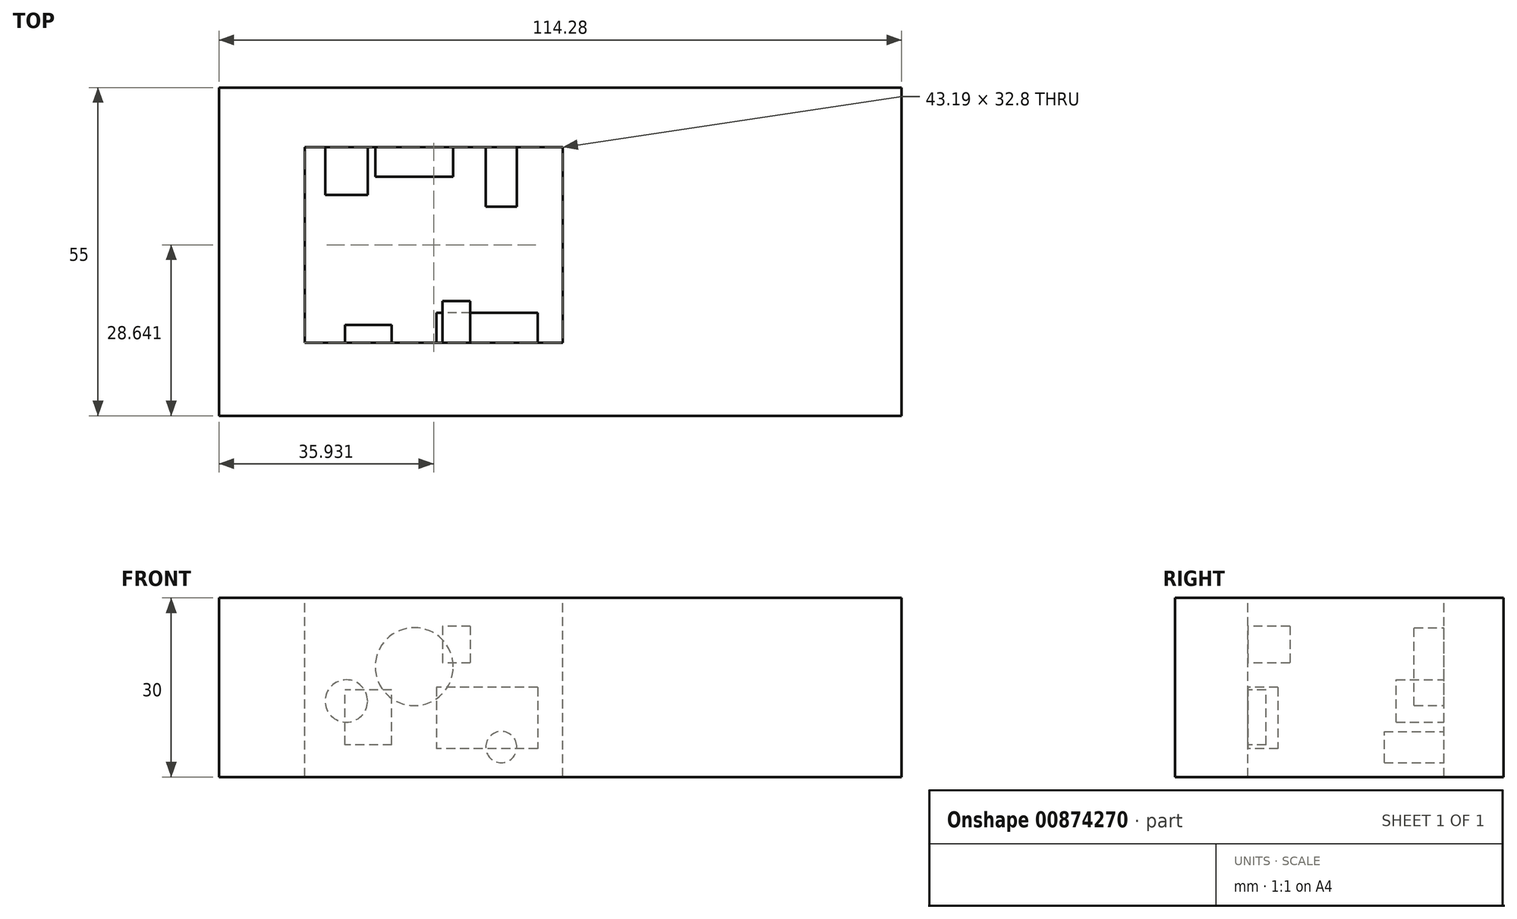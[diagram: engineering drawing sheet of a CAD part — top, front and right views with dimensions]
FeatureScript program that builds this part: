
annotation { "Feature Type Name" : "Feature", "Feature Type Description" : "" }
export const myFeature = defineFeature(function(context is Context, id is Id, definition is map)
    precondition{}
    {
        {
            var Q0;
            Q0=qCreatedBy(makeId("Top.planeOp"),FACE);
            var sketch = newSketch(context, id + "F0", { "sketchPlane" : qUnion([Q0])});
            skLineSegment(sketch, "E0.bottom", {"start": v(-114.28, 55) * mm, "end": v(0, 55) * mm});
            skLineSegment(sketch, "E0.top", {"start": v(-114.28, 0) * mm, "end": v(0, 0) * mm});
            skLineSegment(sketch, "E0.left", {"start": v(-114.28, 55) * mm, "end": v(-114.28, 0) * mm});
            skLineSegment(sketch, "E0.right", {"start": v(0, 55) * mm, "end": v(0, 0) * mm});
            skSolve(sketch);
        }
        {
            var Q0;
            Q0=makeQuery(id+"F0.imprint","IMPRINT",FACE,{"disambiguationData":[TD([[makeQuery(id+"F0.imprint","IMPRINT",EDGE,{"derivedFrom":sQuery(id+"F0.wireOp",EDGE,"E0.bottom")}),-1.0]])]});
            extrude(context, id + "F1", {"entities" : qUnion([Q0]), "depth" : 30 * mm, "offsetDistance" : 25 * mm});
        }
        {
            var Q0;
            Q0=makeQuery(id+"F1.opExtrude","CAP_FACE",FACE,{"disambiguationData":[OSD([sQuery(id+"F0.wireOp",EDGE,"E0.bottom"),sQuery(id+"F0.wireOp",EDGE,"E0.top"),sQuery(id+"F0.wireOp",EDGE,"E0.left"),sQuery(id+"F0.wireOp",EDGE,"E0.right")])],"isStart":false});
            var sketch = newSketch(context, id + "F2", { "sketchPlane" : qUnion([Q0])});
            skLineSegment(sketch, "E1.bottom", {"start": v(-99.94, 45.04) * mm, "end": v(-56.75, 45.04) * mm});
            skLineSegment(sketch, "E1.top", {"start": v(-99.94, 12.24) * mm, "end": v(-56.75, 12.24) * mm});
            skLineSegment(sketch, "E1.left", {"start": v(-99.94, 45.04) * mm, "end": v(-99.94, 12.24) * mm});
            skLineSegment(sketch, "E1.right", {"start": v(-56.75, 45.04) * mm, "end": v(-56.75, 12.24) * mm});
            skSolve(sketch);
        }
        {
            var Q0;
            Q0=makeQuery(id+"F2.imprint","IMPRINT",FACE,{"disambiguationData":[TD([[makeQuery(id+"F2.imprint","IMPRINT",EDGE,{"derivedFrom":sQuery(id+"F2.wireOp",EDGE,"E1.bottom")}),-1.0]])]});
            extrude(context, id + "F3", {"entities" : qUnion([Q0]), "operationType" : NewBodyOperationType.REMOVE, "endBound" : BoundingType.THROUGH_ALL, "oppositeDirection" : true, "depth" : 50 * mm, "offsetDistance" : 25 * mm});
        }
        {
            var Q0;
            Q0=makeQuery(id+"F3.boolean.opBoolean","COPY",FACE,{"derivedFrom":makeQuery(id+"F3.opExtrude","SWEPT_FACE",FACE,{"disambiguationData":[OSD([sQuery(id+"F2.wireOp",EDGE,"E1.top")])]})});
            var sketch = newSketch(context, id + "F4", { "sketchPlane" : qUnion([Q0])});
            skLineSegment(sketch, "E2.bottom", {"start": v(60.98, 23.72) * mm, "end": v(67.38, 23.72) * mm});
            skLineSegment(sketch, "E2.top", {"start": v(60.98, 16.5) * mm, "end": v(67.38, 16.5) * mm});
            skLineSegment(sketch, "E2.left", {"start": v(60.98, 23.72) * mm, "end": v(60.98, 16.5) * mm});
            skLineSegment(sketch, "E2.right", {"start": v(67.38, 23.72) * mm, "end": v(67.38, 16.5) * mm});
            skLineSegment(sketch, "E3.bottom", {"start": v(69.37, 8.04) * mm, "end": v(73.93, 8.04) * mm});
            skLineSegment(sketch, "E3.top", {"start": v(69.37, 13.28) * mm, "end": v(73.93, 13.28) * mm});
            skLineSegment(sketch, "E3.left", {"start": v(69.37, 8.04) * mm, "end": v(69.37, 13.28) * mm});
            skLineSegment(sketch, "E3.right", {"start": v(73.93, 8.04) * mm, "end": v(73.93, 13.28) * mm});
            skLineSegment(sketch, "E4.bottom", {"start": v(79.93, 18.19) * mm, "end": v(85.7, 18.19) * mm});
            skLineSegment(sketch, "E4.top", {"start": v(79.93, 25.53) * mm, "end": v(85.7, 25.53) * mm});
            skLineSegment(sketch, "E4.left", {"start": v(79.93, 18.19) * mm, "end": v(79.93, 25.53) * mm});
            skLineSegment(sketch, "E4.right", {"start": v(85.7, 18.19) * mm, "end": v(85.7, 25.53) * mm});
            skLineSegment(sketch, "E5.bottom", {"start": v(85.35, 5.38) * mm, "end": v(93.17, 5.38) * mm});
            skLineSegment(sketch, "E5.top", {"start": v(85.35, 14.6) * mm, "end": v(93.17, 14.6) * mm});
            skLineSegment(sketch, "E5.left", {"start": v(85.35, 5.38) * mm, "end": v(85.35, 14.6) * mm});
            skLineSegment(sketch, "E5.right", {"start": v(93.17, 5.38) * mm, "end": v(93.17, 14.6) * mm});
            skLineSegment(sketch, "E6.bottom", {"start": v(93.3, 23.36) * mm, "end": v(96.27, 23.36) * mm});
            skLineSegment(sketch, "E6.top", {"start": v(93.3, 19.33) * mm, "end": v(96.27, 19.33) * mm});
            skLineSegment(sketch, "E6.left", {"start": v(93.3, 23.36) * mm, "end": v(93.3, 19.33) * mm});
            skLineSegment(sketch, "E6.right", {"start": v(96.27, 23.36) * mm, "end": v(96.27, 19.33) * mm});
            skSolve(sketch);
        }
        {
            var Q0;
            Q0=makeQuery(id+"F4.imprint","IMPRINT",FACE,{"disambiguationData":[TD([[makeQuery(id+"F4.imprint","IMPRINT",EDGE,{"derivedFrom":sQuery(id+"F4.wireOp",EDGE,"E5.bottom")}),1.0]])]});
            extrude(context, id + "F5", {"entities" : qUnion([Q0]), "operationType" : NewBodyOperationType.ADD, "depth" : 3 * mm, "offsetDistance" : 25 * mm});
        }
        {
            var Q0;
            Q0=makeQuery(id+"F3.boolean.opBoolean","COPY",FACE,{"derivedFrom":makeQuery(id+"F3.opExtrude","SWEPT_FACE",FACE,{"disambiguationData":[OSD([sQuery(id+"F2.wireOp",EDGE,"E1.top")])]})});
            var sketch = newSketch(context, id + "F6", { "sketchPlane" : qUnion([Q0])});
            skLineSegment(sketch, "E7.bottom", {"start": v(72.2, 25.26) * mm, "end": v(76.89, 25.26) * mm});
            skLineSegment(sketch, "E7.top", {"start": v(72.2, 19.07) * mm, "end": v(76.89, 19.07) * mm});
            skLineSegment(sketch, "E7.left", {"start": v(72.2, 25.26) * mm, "end": v(72.2, 19.07) * mm});
            skLineSegment(sketch, "E7.right", {"start": v(76.89, 25.26) * mm, "end": v(76.89, 19.07) * mm});
            skSolve(sketch);
        }
        {
            var Q0;
            Q0 = qSketchRegion(id + "F6", true);
            extrude(context, id + "F7", {"entities" : qUnion([Q0]), "operationType" : NewBodyOperationType.ADD, "depth" : 7 * mm, "offsetDistance" : 25 * mm});
        }
        {
            var Q0;
            Q0=makeQuery(id+"F3.boolean.opBoolean","COPY",FACE,{"derivedFrom":makeQuery(id+"F3.opExtrude","SWEPT_FACE",FACE,{"disambiguationData":[OSD([sQuery(id+"F2.wireOp",EDGE,"E1.top")])]})});
            var sketch = newSketch(context, id + "F8", { "sketchPlane" : qUnion([Q0])});
            skLineSegment(sketch, "E8.bottom", {"start": v(60.93, 15.02) * mm, "end": v(77.86, 15.02) * mm});
            skLineSegment(sketch, "E8.top", {"start": v(60.93, 4.76) * mm, "end": v(77.86, 4.76) * mm});
            skLineSegment(sketch, "E8.left", {"start": v(60.93, 15.02) * mm, "end": v(60.93, 4.76) * mm});
            skLineSegment(sketch, "E8.right", {"start": v(77.86, 15.02) * mm, "end": v(77.86, 4.76) * mm});
            skSolve(sketch);
        }
        {
            var Q0;
            Q0 = qSketchRegion(id + "F8", true);
            extrude(context, id + "F9", {"entities" : qUnion([Q0]), "operationType" : NewBodyOperationType.ADD, "depth" : 5 * mm, "offsetDistance" : 25 * mm});
        }
        {
            var Q0;
            Q0=makeQuery(id+"F3.boolean.opBoolean","COPY",FACE,{"derivedFrom":makeQuery(id+"F3.opExtrude","SWEPT_FACE",FACE,{"disambiguationData":[OSD([sQuery(id+"F2.wireOp",EDGE,"E1.bottom")])]})});
            var sketch = newSketch(context, id + "F10", { "sketchPlane" : qUnion([Q0])});
            skCircle(sketch, "E9", {"center": v(-92.95, 12.72) * mm, "radius": 3.56 * mm});
            skSolve(sketch);
        }
        {
            var Q0;
            Q0 = qSketchRegion(id + "F10", true);
            extrude(context, id + "F11", {"entities" : qUnion([Q0]), "operationType" : NewBodyOperationType.ADD, "depth" : 8 * mm, "offsetDistance" : 25 * mm});
        }
        {
            var Q0;
            Q0=makeQuery(id+"F3.boolean.opBoolean","COPY",FACE,{"derivedFrom":makeQuery(id+"F3.opExtrude","SWEPT_FACE",FACE,{"disambiguationData":[OSD([sQuery(id+"F2.wireOp",EDGE,"E1.bottom")])]})});
            var sketch = newSketch(context, id + "F12", { "sketchPlane" : qUnion([Q0])});
            skCircle(sketch, "E10", {"center": v(-81.59, 18.47) * mm, "radius": 6.52 * mm});
            skSolve(sketch);
        }
        {
            var Q0;
            Q0 = qSketchRegion(id + "F12", true);
            extrude(context, id + "F13", {"entities" : qUnion([Q0]), "operationType" : NewBodyOperationType.ADD, "depth" : 5 * mm, "offsetDistance" : 25 * mm});
        }
        {
            var Q0;
            Q0=makeQuery(id+"F3.boolean.opBoolean","COPY",FACE,{"derivedFrom":makeQuery(id+"F3.opExtrude","SWEPT_FACE",FACE,{"disambiguationData":[OSD([sQuery(id+"F2.wireOp",EDGE,"E1.bottom")])]})});
            var sketch = newSketch(context, id + "F14", { "sketchPlane" : qUnion([Q0])});
            skCircle(sketch, "E11", {"center": v(-67.02, 5) * mm, "radius": 2.62 * mm});
            skSolve(sketch);
        }
        {
            var Q0;
            Q0 = qSketchRegion(id + "F14", true);
            extrude(context, id + "F15", {"entities" : qUnion([Q0]), "operationType" : NewBodyOperationType.ADD, "depth" : 10 * mm, "offsetDistance" : 25 * mm});
        }
    });
